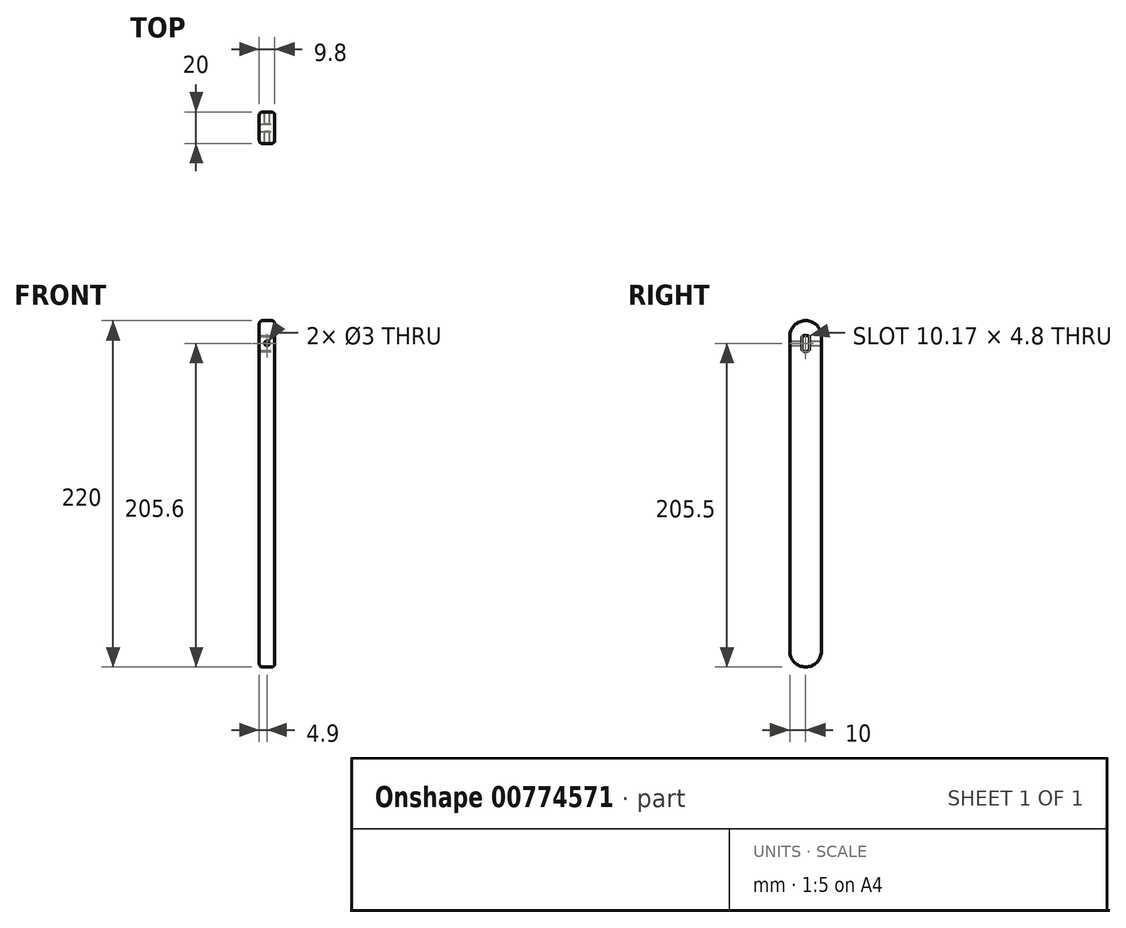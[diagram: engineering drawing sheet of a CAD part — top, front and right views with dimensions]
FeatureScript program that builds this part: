
annotation { "Feature Type Name" : "Feature", "Feature Type Description" : "" }
export const myFeature = defineFeature(function(context is Context, id is Id, definition is map)
    precondition{}
    {
        {
            var Q0;
            Q0=qCreatedBy(makeId("Right.planeOp"),FACE);
            var sketch = newSketch(context, id + "F0", { "sketchPlane" : qUnion([Q0])});
            skLineSegment(sketch, "E0", {"start": v(0, 40.08) * mm, "end": v(0, -50) * mm, "construction": true});
            skLineSegment(sketch, "E1", {"start": v(-74.73, 0) * mm, "end": v(69.05, 0) * mm, "construction": true});
            skLineSegment(sketch, "E2.bottom", {"start": v(0, 0) * mm, "end": v(-10, 0) * mm});
            skLineSegment(sketch, "E2.top", {"start": v(0, 100) * mm, "end": v(-10, 100) * mm});
            skLineSegment(sketch, "E2.left", {"start": v(0, 0) * mm, "end": v(0, 100) * mm});
            skLineSegment(sketch, "E2.right", {"start": v(-10, 0) * mm, "end": v(-10, 100) * mm});
            skArc(sketch, "E3", {"start": v(-10, 100) * mm, "mid": v(-7.07, 107.07) * mm, "end": v(0, 110) * mm});
            skLineSegment(sketch, "E4.MirrorCS", {"start": v(10, 0) * mm, "end": v(10, 100) * mm});
            skLineSegment(sketch, "E5.MirrorCS", {"start": v(0, 0) * mm, "end": v(10, 0) * mm});
            skArc(sketch, "E6.MirrorCS", {"start": v(10, 100) * mm, "mid": v(7.07, 107.07) * mm, "end": v(0, 110) * mm});
            skLineSegment(sketch, "E7.MirrorCS", {"start": v(0, 100) * mm, "end": v(10, 100) * mm});
            skLineSegment(sketch, "E8.MirrorCS", {"start": v(0, 0) * mm, "end": v(0, -100) * mm});
            skLineSegment(sketch, "E9.MirrorCS", {"start": v(0, -100) * mm, "end": v(-10, -100) * mm});
            skLineSegment(sketch, "E10.MirrorCS", {"start": v(-10, 0) * mm, "end": v(-10, -100) * mm});
            skLineSegment(sketch, "E11.MirrorCS", {"start": v(0, -100) * mm, "end": v(10, -100) * mm});
            skArc(sketch, "E12.MirrorCS", {"start": v(-10, -100) * mm, "mid": v(-7.07, -107.07) * mm, "end": v(0, -110) * mm});
            skArc(sketch, "E13.MirrorCS", {"start": v(10, -100) * mm, "mid": v(7.07, -107.07) * mm, "end": v(0, -110) * mm});
            skLineSegment(sketch, "E14.MirrorCS", {"start": v(10, 0) * mm, "end": v(10, -100) * mm});
            skSolve(sketch);
        }
        {
            var Q0;
            Q0 = qSketchRegion(id + "F0", true);
            extrude(context, id + "F1", {"entities" : qUnion([Q0]), "depth" : 9.8 * mm, "offsetDistance" : 25 * mm});
        }
        {
            var Q0;
            Q0=makeQuery(id+"F1.opExtrude","CAP_FACE",FACE,{"disambiguationData":[OSD([sQuery(id+"F0.wireOp",EDGE,"E2.right"),sQuery(id+"F0.wireOp",EDGE,"E3"),sQuery(id+"F0.wireOp",EDGE,"E4.MirrorCS"),sQuery(id+"F0.wireOp",EDGE,"E6.MirrorCS"),sQuery(id+"F0.wireOp",EDGE,"E10.MirrorCS"),sQuery(id+"F0.wireOp",EDGE,"E12.MirrorCS"),sQuery(id+"F0.wireOp",EDGE,"E13.MirrorCS"),sQuery(id+"F0.wireOp",EDGE,"E14.MirrorCS")])],"isStart":false});
            var sketch = newSketch(context, id + "F2", { "sketchPlane" : qUnion([Q0])});
            skLineSegment(sketch, "E15.bottom", {"start": v(2.4, 91) * mm, "end": v(-2.4, 91) * mm});
            skLineSegment(sketch, "E15.top", {"start": v(2.4, 100) * mm, "end": v(-2.4, 100) * mm});
            skLineSegment(sketch, "E15.left", {"start": v(2.4, 91) * mm, "end": v(2.4, 100) * mm});
            skLineSegment(sketch, "E15.right", {"start": v(-2.4, 91) * mm, "end": v(-2.4, 100) * mm});
            skPoint(sketch, "E15.middle", {"position": v(0, 95.5) * mm});
            skArc(sketch, "E16", {"start": v(2.4, 100) * mm, "mid": v(0, 100.59) * mm, "end": v(-2.4, 100) * mm});
            skArc(sketch, "E17", {"start": v(-2.4, 91) * mm, "mid": v(0, 90.41) * mm, "end": v(2.4, 91) * mm});
            skLineSegment(sketch, "E18", {"start": v(-10, 100) * mm, "end": v(10, 100) * mm, "construction": true});
            skSolve(sketch);
        }
        {
            var Q0;
            Q0 = qSketchRegion(id + "F2", true);
            extrude(context, id + "F3", {"entities" : qUnion([Q0]), "operationType" : NewBodyOperationType.REMOVE, "flatOperationType" : FlatOperationType.REMOVE, "endBound" : BoundingType.THROUGH_ALL, "oppositeDirection" : true, "depth" : 25 * mm, "offsetDistance" : 25 * mm, "domain" : OperationDomain.MODEL});
        }
        {
            var Q0;
            Q0=makeQuery(id+"F1.opExtrude","SWEPT_FACE",FACE,{"disambiguationData":[OSD([sQuery(id+"F0.wireOp",EDGE,"E4.MirrorCS"),sQuery(id+"F0.wireOp",EDGE,"E14.MirrorCS")])]});
            var sketch = newSketch(context, id + "F4", { "sketchPlane" : qUnion([Q0])});
            skCircle(sketch, "E19", {"center": v(-4.9, 95.6) * mm, "radius": 1.5 * mm});
            skPoint(sketch, "E19.centerSnap0", {"position": v(-4.9, 100) * mm});
            skSolve(sketch);
        }
        {
            var Q0;
            Q0 = qSketchRegion(id + "F4", true);
            extrude(context, id + "F5", {"entities" : qUnion([Q0]), "operationType" : NewBodyOperationType.REMOVE, "endBound" : BoundingType.THROUGH_ALL, "oppositeDirection" : true, "depth" : 25 * mm, "offsetDistance" : 25 * mm});
        }
        {
            var Q0;
            Q0=makeQuery(id+"F1.opExtrude","CAP_EDGE",EDGE,{"disambiguationData":[OSD([sQuery(id+"F0.wireOp",EDGE,"E2.right"),sQuery(id+"F0.wireOp",EDGE,"E10.MirrorCS")])],"isStart":false});
            fillet(context, id + "F6", {"entities" : qUnion([Q0]), "radius" : 2 * mm, "tangentPropagation" : true, "allowEdgeOverflow" : false});
        }
        {
            var Q0;
            Q0=makeQuery(id+"F1.opExtrude","CAP_EDGE",EDGE,{"disambiguationData":[OSD([sQuery(id+"F0.wireOp",EDGE,"E2.right"),sQuery(id+"F0.wireOp",EDGE,"E10.MirrorCS")])],"isStart":true});
            fillet(context, id + "F7", {"entities" : qUnion([Q0]), "radius" : 2 * mm, "tangentPropagation" : true, "allowEdgeOverflow" : false});
        }
    });
